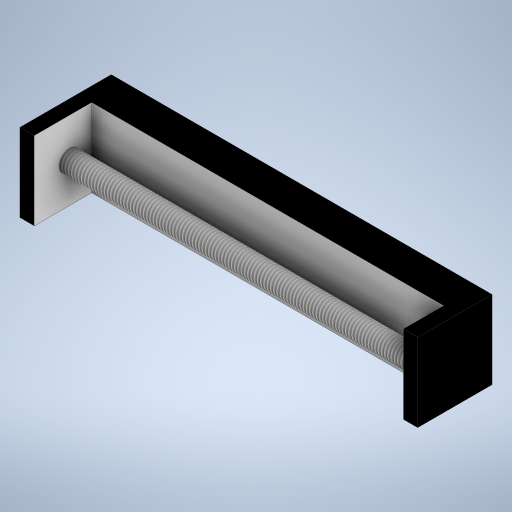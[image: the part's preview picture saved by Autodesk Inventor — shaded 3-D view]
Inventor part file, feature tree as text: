
AUTODESK INVENTOR PART (.ipt)
format: ipt  version: 2023 (Build 270158000, 158)  size: 299,008 bytes
history: native  units: in
note: dims shown in document units (in); Inventor stores cm internally (conversion verified against a paired STEP export)
features: extrude x5, sketch x2, thread x2
ambient origin geometry x8: Origin, YZ Plane, XZ Plane, XY Plane, X Axis, Y Axis, Z Axis, Center Point
bodies: Solid1 (feature_tree)
feature tree (9):
  extrude  "Extrusion1"  Depth=1.1811in
  sketch  "Sketch2"  dims[d2=0.5118in d3=0.0in d4=0.2165in d5=0.2165in d6=0.8661in d7=0.0in d8=0.6102in d9=0.0in d10=0.3543in d11=2.0079in d12=0.0in d13=4.8819in d14=0.0in d21=0.374in d22=0.1575in d23=0.6102in d24=0.0in d25=5.315in d26=0.0in]
  extrude  "Extrusion2"  Depth=0.2165in
  extrude  "Extrusion3"  Depth=0.2165in
  extrude  "Extrusion7"  Depth=0.8661in TaperAngle=0.0deg
  thread  "Thread2"  [1 undecoded]
  extrude  "Extrusion4"  Depth=5.315in
  thread  "Thread1"  [1 undecoded]
  sketch  "Sketch1"  dims[d0=5.748in d1=1.1811in]
note: 2 required parameter values undecoded (feature->parameter linkage not recoverable at this tier; creation-order binding heuristic only, values carry confidence <= 0.55)
